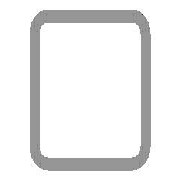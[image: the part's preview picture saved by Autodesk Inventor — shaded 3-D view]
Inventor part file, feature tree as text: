
AUTODESK INVENTOR PART (.ipt)
format: ipt  version: 2025 (Build 290162010, 162A)  size: 142,848 bytes
history: native  units: mm (DEFAULTED — no unit token found)
features: other x4, sketch x1, plane x1
ambient origin geometry x8: Origin, YZ Plane, XZ Plane, XY Plane, X Axis, Y Axis, Z Axis, Center Point
bodies: Solid1 (feature_tree), Body (feature_tree)
feature tree (6):
  parser-record x1  (decoder bookkeeping rows leaked as tree rows — omitted from the tree; the rows remain in map.json)
  other  "Driven Length"
  other  "Start Plane"
  other  "End Plane"
  sketch  "Sketch3"  dims[d3=635.0mm d4=0.0mm d7=4.0mm d9=40.0mm d11=40.0mm d12=2.0mm d13=100.0mm d14=735.0mm d15=20.0mm d16=20.0mm d17=90.0deg d18=635.0mm]
  plane  "Work Plane3"
